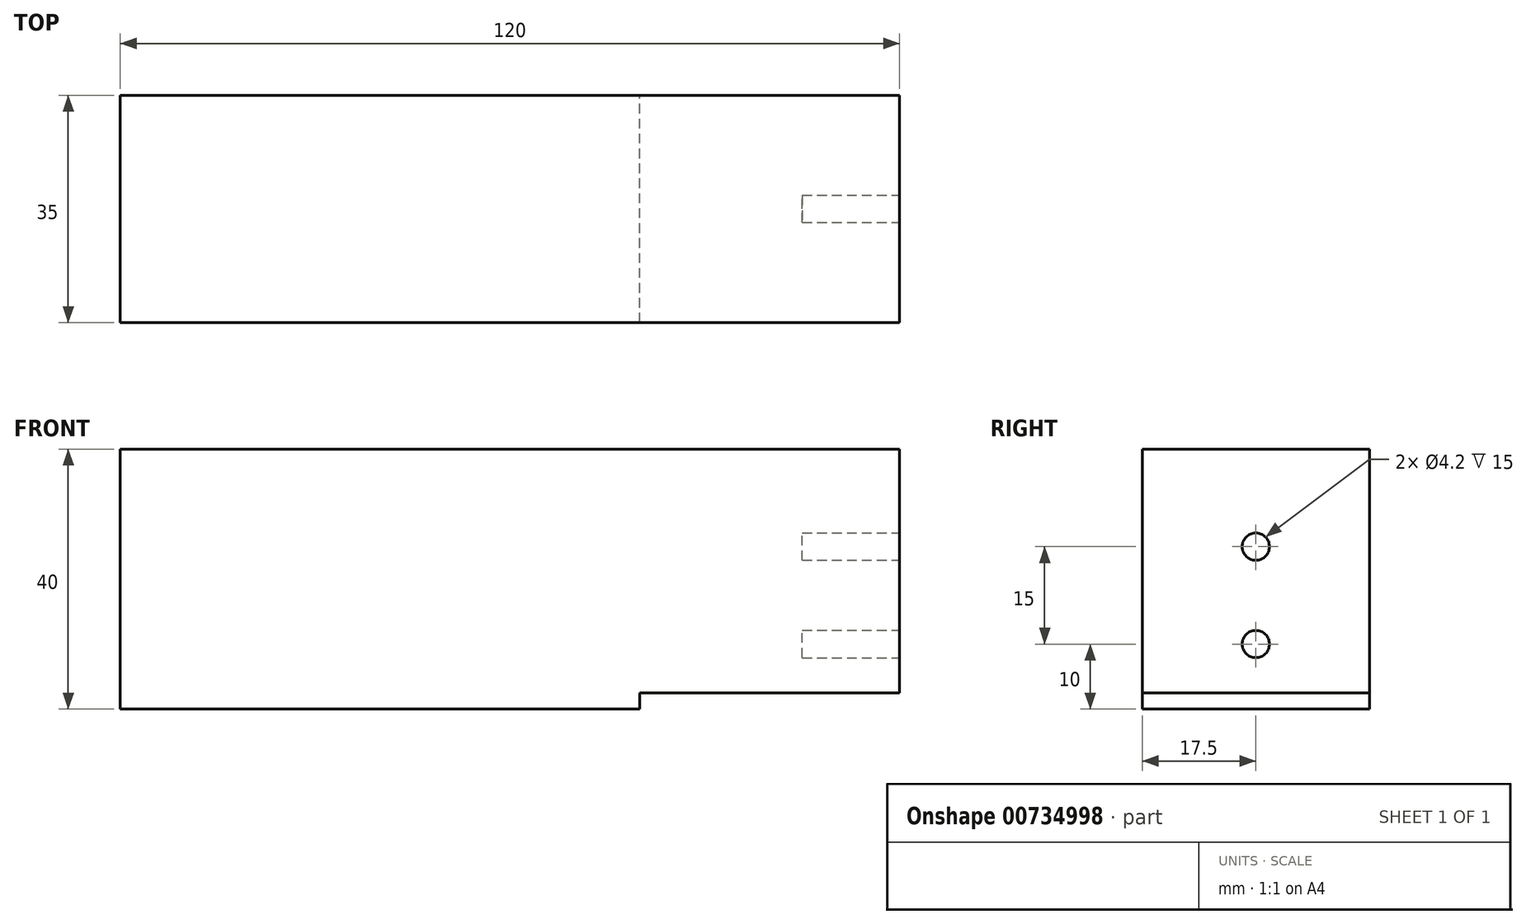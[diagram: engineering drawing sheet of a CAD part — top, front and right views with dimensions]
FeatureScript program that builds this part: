
annotation { "Feature Type Name" : "Feature", "Feature Type Description" : "" }
export const myFeature = defineFeature(function(context is Context, id is Id, definition is map)
    precondition{}
    {
        {
            var Q0;
            Q0=qCreatedBy(makeId("Top.planeOp"),FACE);
            var sketch = newSketch(context, id + "F0", { "sketchPlane" : qUnion([Q0])});
            skLineSegment(sketch, "E0.bottom", {"start": v(0, 0) * mm, "end": v(-120, 0) * mm});
            skLineSegment(sketch, "E0.top", {"start": v(0, 35) * mm, "end": v(-120, 35) * mm});
            skLineSegment(sketch, "E0.left", {"start": v(0, 0) * mm, "end": v(0, 35) * mm});
            skLineSegment(sketch, "E0.right", {"start": v(-120, 0) * mm, "end": v(-120, 35) * mm});
            skSolve(sketch);
        }
        {
            var Q0;
            Q0 = qSketchRegion(id + "F0", true);
            extrude(context, id + "F1", {"entities" : qUnion([Q0]), "depth" : 40 * mm, "offsetDistance" : 25 * mm});
        }
        {
            var Q0;
            Q0=makeQuery(id+"F1.opExtrude","SWEPT_FACE",FACE,{"disambiguationData":[OSD([sQuery(id+"F0.wireOp",EDGE,"E0.left")])]});
            var sketch = newSketch(context, id + "F2", { "sketchPlane" : qUnion([Q0])});
            skLineSegment(sketch, "E1", {"start": v(17.5, 0) * mm, "end": v(17.5, 10) * mm});
            skLineSegment(sketch, "E2", {"start": v(17.5, 10) * mm, "end": v(17.5, 25) * mm});
            skCircle(sketch, "E3", {"center": v(17.5, 25) * mm, "radius": 2.1 * mm});
            skCircle(sketch, "E4", {"center": v(17.5, 10) * mm, "radius": 2.1 * mm});
            skSolve(sketch);
        }
        {
            var Q0;
            Q0 = qSketchRegion(id + "F2", true);
            extrude(context, id + "F3", {"entities" : qUnion([Q0]), "operationType" : NewBodyOperationType.REMOVE, "oppositeDirection" : true, "depth" : 15 * mm, "offsetDistance" : 25 * mm});
        }
        {
            var Q0;
            Q0=makeQuery(id+"F1.opExtrude","SWEPT_FACE",FACE,{"disambiguationData":[OSD([sQuery(id+"F0.wireOp",EDGE,"E0.left")])]});
            var sketch = newSketch(context, id + "F4", { "sketchPlane" : qUnion([Q0])});
            skLineSegment(sketch, "E5.bottom", {"start": v(0, 0) * mm, "end": v(35, 0) * mm});
            skLineSegment(sketch, "E5.top", {"start": v(0, 2.5) * mm, "end": v(35, 2.5) * mm});
            skLineSegment(sketch, "E5.left", {"start": v(0, 0) * mm, "end": v(0, 2.5) * mm});
            skLineSegment(sketch, "E5.right", {"start": v(35, 0) * mm, "end": v(35, 2.5) * mm});
            skSolve(sketch);
        }
        {
            var Q0;
            Q0 = qSketchRegion(id + "F4", true);
            extrude(context, id + "F5", {"entities" : qUnion([Q0]), "operationType" : NewBodyOperationType.REMOVE, "oppositeDirection" : true, "depth" : 40 * mm, "offsetDistance" : 25 * mm});
        }
    });
